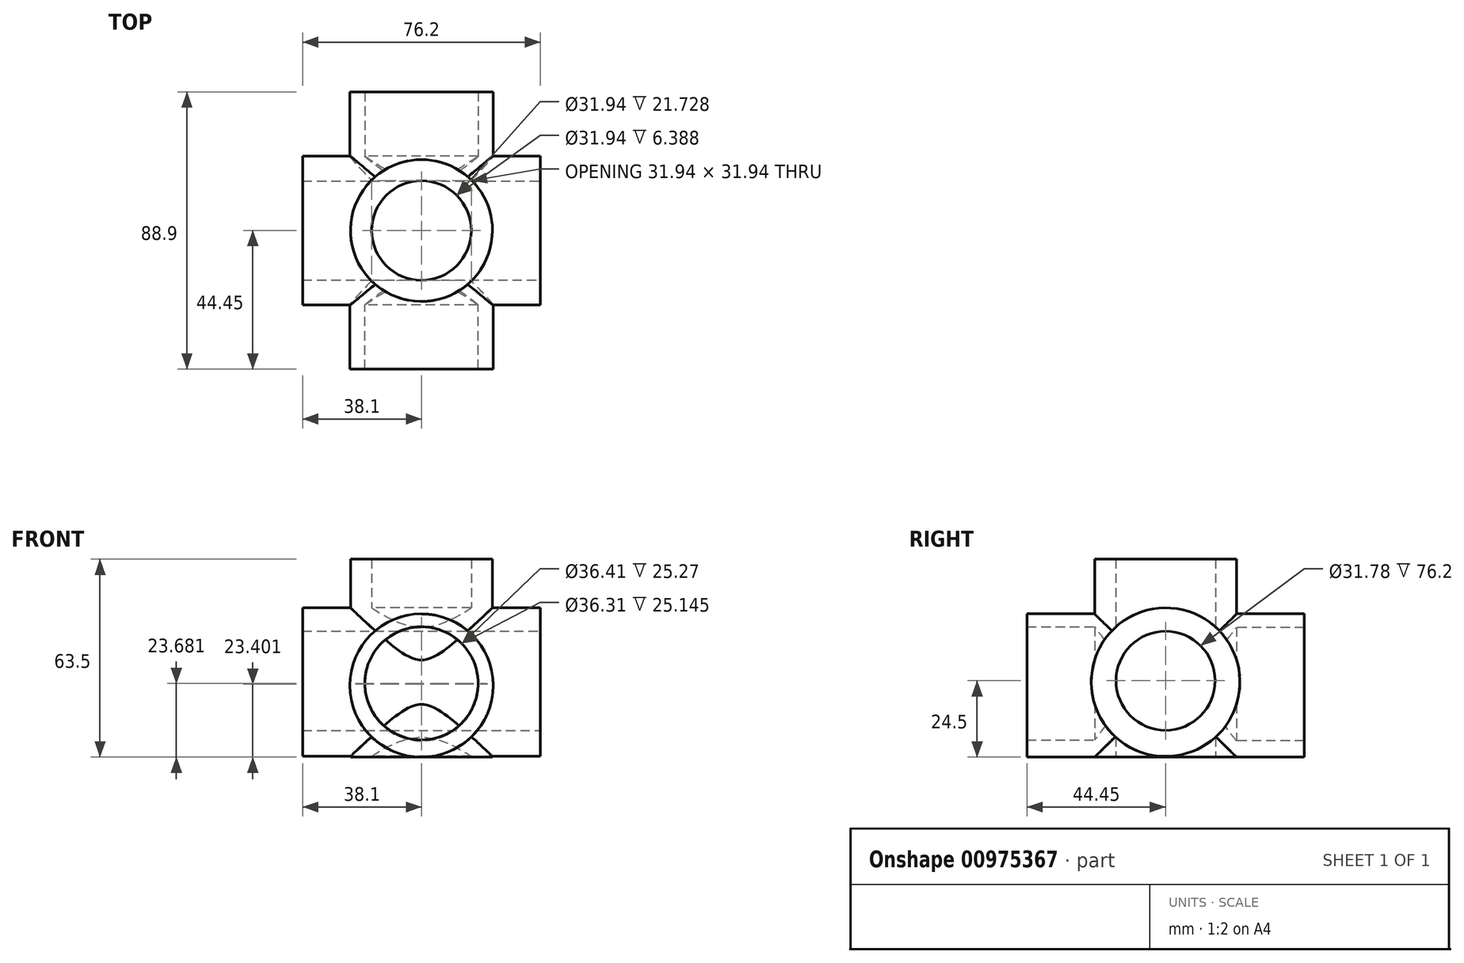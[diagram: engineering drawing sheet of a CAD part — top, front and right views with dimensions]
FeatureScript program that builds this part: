
annotation { "Feature Type Name" : "Feature", "Feature Type Description" : "" }
export const myFeature = defineFeature(function(context is Context, id is Id, definition is map)
    precondition{}
    {
        {
            var Q0;
            Q0=qCreatedBy(makeId("Front.planeOp"),FACE);
            var sketch = newSketch(context, id + "F0", { "sketchPlane" : qUnion([Q0])});
            skCircle(sketch, "E0", {"center": v(0, 22.98) * mm, "radius": 22.98 * mm});
            skSolve(sketch);
        }
        {
            var Q0;
            Q0 = qSketchRegion(id + "F0", true);
            extrude(context, id + "F1", {"entities" : qUnion([Q0]), "depth" : 44.45 * mm, "offsetDistance" : 25.4 * mm, "hasSecondDirection" : true, "secondDirectionOppositeDirection" : true, "secondDirectionDepth" : 44.45 * mm});
        }
        {
            var Q0;
            Q0=qCreatedBy(makeId("Front.planeOp"),FACE);
            var sketch = newSketch(context, id + "F2", { "sketchPlane" : qUnion([Q0])});
            skCircle(sketch, "E1", {"center": v(0, 23.4) * mm, "radius": 18.2 * mm});
            skSolve(sketch);
        }
        {
            var Q0;
            Q0 = qSketchRegion(id + "F2", true);
            extrude(context, id + "F3", {"entities" : qUnion([Q0]), "operationType" : NewBodyOperationType.REMOVE, "oppositeDirection" : true, "depth" : 44.45 * mm, "offsetDistance" : 25.4 * mm});
        }
        {
            var Q0;
            Q0=qCreatedBy(makeId("Front.planeOp"),FACE);
            var sketch = newSketch(context, id + "F4", { "sketchPlane" : qUnion([Q0])});
            skCircle(sketch, "E2", {"center": v(0, 23.68) * mm, "radius": 18.16 * mm});
            skSolve(sketch);
        }
        {
            var Q0;
            Q0 = qSketchRegion(id + "F4", true);
            extrude(context, id + "F5", {"entities" : qUnion([Q0]), "operationType" : NewBodyOperationType.REMOVE, "depth" : 44.45 * mm, "offsetDistance" : 25.4 * mm});
        }
        {
            var Q0;
            Q0=qCreatedBy(makeId("Top.planeOp"),FACE);
            var sketch = newSketch(context, id + "F6", { "sketchPlane" : qUnion([Q0])});
            skCircle(sketch, "E3", {"center": v(0, 0) * mm, "radius": 22.75 * mm});
            skSolve(sketch);
        }
        {
            var Q0;
            Q0 = qSketchRegion(id + "F6", true);
            extrude(context, id + "F7", {"entities" : qUnion([Q0]), "operationType" : NewBodyOperationType.ADD, "depth" : 63.5 * mm, "offsetDistance" : 25.4 * mm});
        }
        {
            var Q0;
            Q0=qCreatedBy(makeId("Top.planeOp"),FACE);
            var sketch = newSketch(context, id + "F8", { "sketchPlane" : qUnion([Q0])});
            skCircle(sketch, "E4", {"center": v(0, 0) * mm, "radius": 15.97 * mm});
            skSolve(sketch);
        }
        {
            var Q0;
            Q0 = qSketchRegion(id + "F8", true);
            extrude(context, id + "F9", {"entities" : qUnion([Q0]), "operationType" : NewBodyOperationType.REMOVE, "depth" : 69.85 * mm, "offsetDistance" : 25.4 * mm});
        }
        {
            var Q0;
            Q0=qCreatedBy(makeId("Right.planeOp"),FACE);
            var sketch = newSketch(context, id + "F10", { "sketchPlane" : qUnion([Q0])});
            skCircle(sketch, "E5", {"center": v(0, 24.08) * mm, "radius": 23.84 * mm});
            skSolve(sketch);
        }
        {
            var Q0;
            Q0 = qSketchRegion(id + "F10", true);
            extrude(context, id + "F11", {"entities" : qUnion([Q0]), "operationType" : NewBodyOperationType.ADD, "depth" : 38.1 * mm, "offsetDistance" : 25.4 * mm, "hasSecondDirection" : true, "secondDirectionOppositeDirection" : true, "secondDirectionDepth" : 38.1 * mm});
        }
        {
            var Q0;
            Q0=qCreatedBy(makeId("Right.planeOp"),FACE);
            var sketch = newSketch(context, id + "F12", { "sketchPlane" : qUnion([Q0])});
            skCircle(sketch, "E6", {"center": v(0, 24.5) * mm, "radius": 15.9 * mm});
            skSolve(sketch);
        }
        {
            var Q0;
            Q0 = qSketchRegion(id + "F12", true);
            extrude(context, id + "F13", {"entities" : qUnion([Q0]), "operationType" : NewBodyOperationType.REMOVE, "oppositeDirection" : true, "depth" : 39.88 * mm, "offsetDistance" : 25.4 * mm, "hasSecondDirection" : true, "secondDirectionOppositeDirection" : false, "secondDirectionDepth" : 40.64 * mm});
        }
    });
